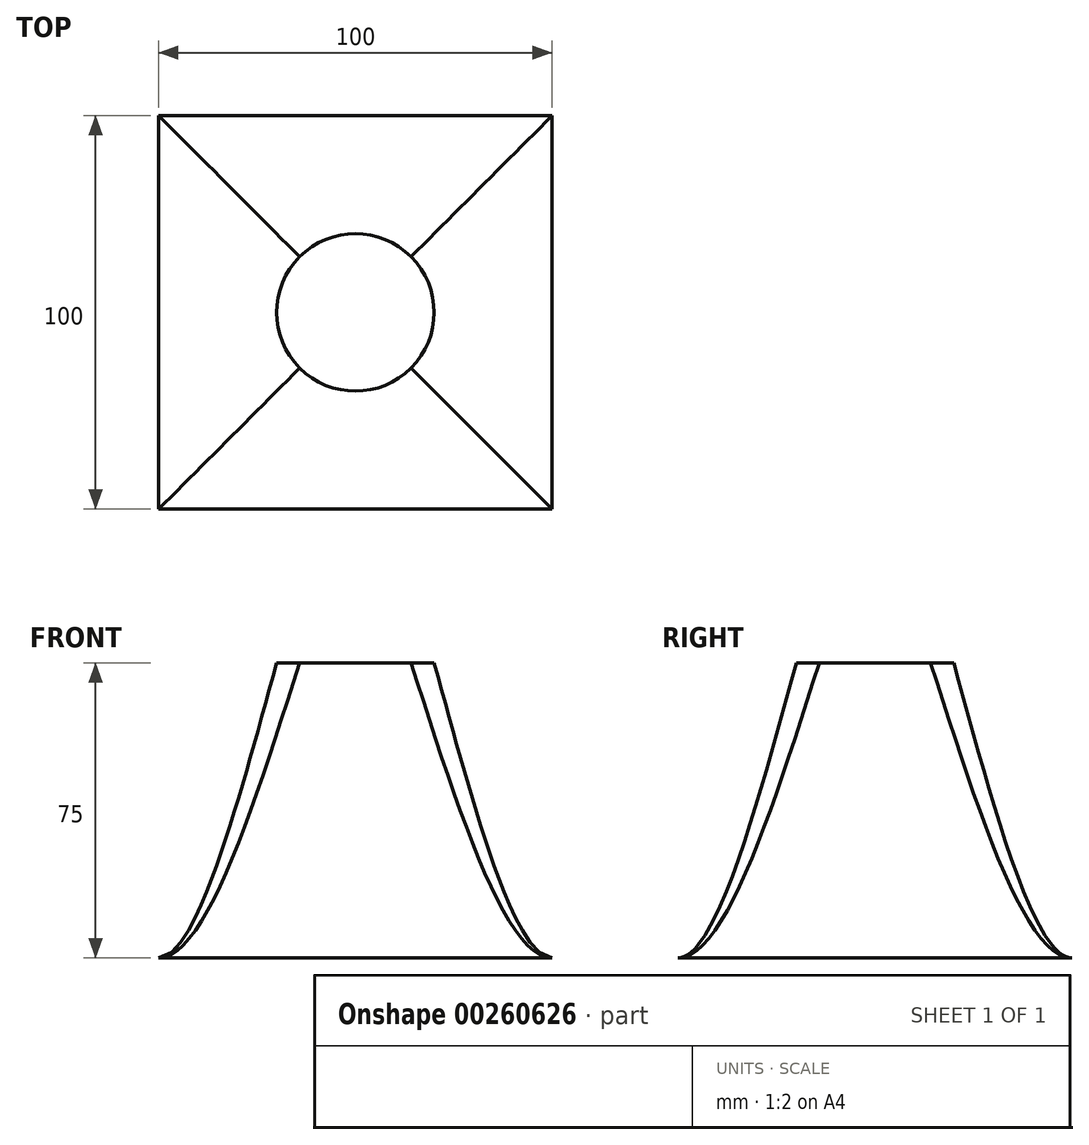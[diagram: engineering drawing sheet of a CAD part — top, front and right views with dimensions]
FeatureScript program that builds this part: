
annotation { "Feature Type Name" : "Feature", "Feature Type Description" : "" }
export const myFeature = defineFeature(function(context is Context, id is Id, definition is map)
    precondition{}
    {
        {
            var Q0;
            Q0=qCreatedBy(makeId("Top.planeOp"),FACE);
            var sketch = newSketch(context, id + "F0", { "sketchPlane" : qUnion([Q0])});
            skLineSegment(sketch, "E0.bottom", {"start": v(-50, 50) * mm, "end": v(50, 50) * mm});
            skLineSegment(sketch, "E0.top", {"start": v(-50, -50) * mm, "end": v(50, -50) * mm});
            skLineSegment(sketch, "E0.left", {"start": v(-50, 50) * mm, "end": v(-50, -50) * mm});
            skLineSegment(sketch, "E0.right", {"start": v(50, 50) * mm, "end": v(50, -50) * mm});
            skPoint(sketch, "E0.middle", {"position": v(0, 0) * mm});
            skSolve(sketch);
        }
        {
            var Q0;
            Q0=makeQuery(id+"F0.imprint","IMPRINT",FACE,{"disambiguationData":[TD([[makeQuery(id+"F0.imprint","IMPRINT",EDGE,{"derivedFrom":sQuery(id+"F0.wireOp",EDGE,"E0.bottom")}),-1.0]])]});
            cPlane(context, id + "F1", {"entities" : qUnion([Q0]), "cplaneType" : CPlaneType.OFFSET, "offset" : 75 * mm, "width" : 150 * mm, "height" : 150 * mm});
        }
        {
            var Q0;
            Q0=qCreatedBy(id+"F1.planeOp",FACE);
            var sketch = newSketch(context, id + "F2", { "sketchPlane" : qUnion([Q0])});
            skCircle(sketch, "E1", {"center": v(0, 0) * mm, "radius": 20 * mm});
            skSolve(sketch);
        }
        {
            var Q0;
            Q0=makeQuery(id+"F0.imprint","IMPRINT",FACE,{"disambiguationData":[TD([[makeQuery(id+"F0.imprint","IMPRINT",EDGE,{"derivedFrom":sQuery(id+"F0.wireOp",EDGE,"E0.bottom")}),-1.0]])]});
            var Q1;
            Q1=makeQuery(id+"F2.imprint","IMPRINT",FACE,{"disambiguationData":[TD([[makeQuery(id+"F2.imprint","IMPRINT",EDGE,{"derivedFrom":sQuery(id+"F2.wireOp",EDGE,"E1")}),1.0]])]});
            loft(context, id + "F3", {"startCondition" : LoftEndDerivativeType.TANGENT_TO_PROFILE, "startMagnitude" : 1, "sheetProfilesArray" : [{ "sheetProfileEntities" : qUnion([Q0]) }, { "sheetProfileEntities" : qUnion([Q1]) }]});
        }
    });
